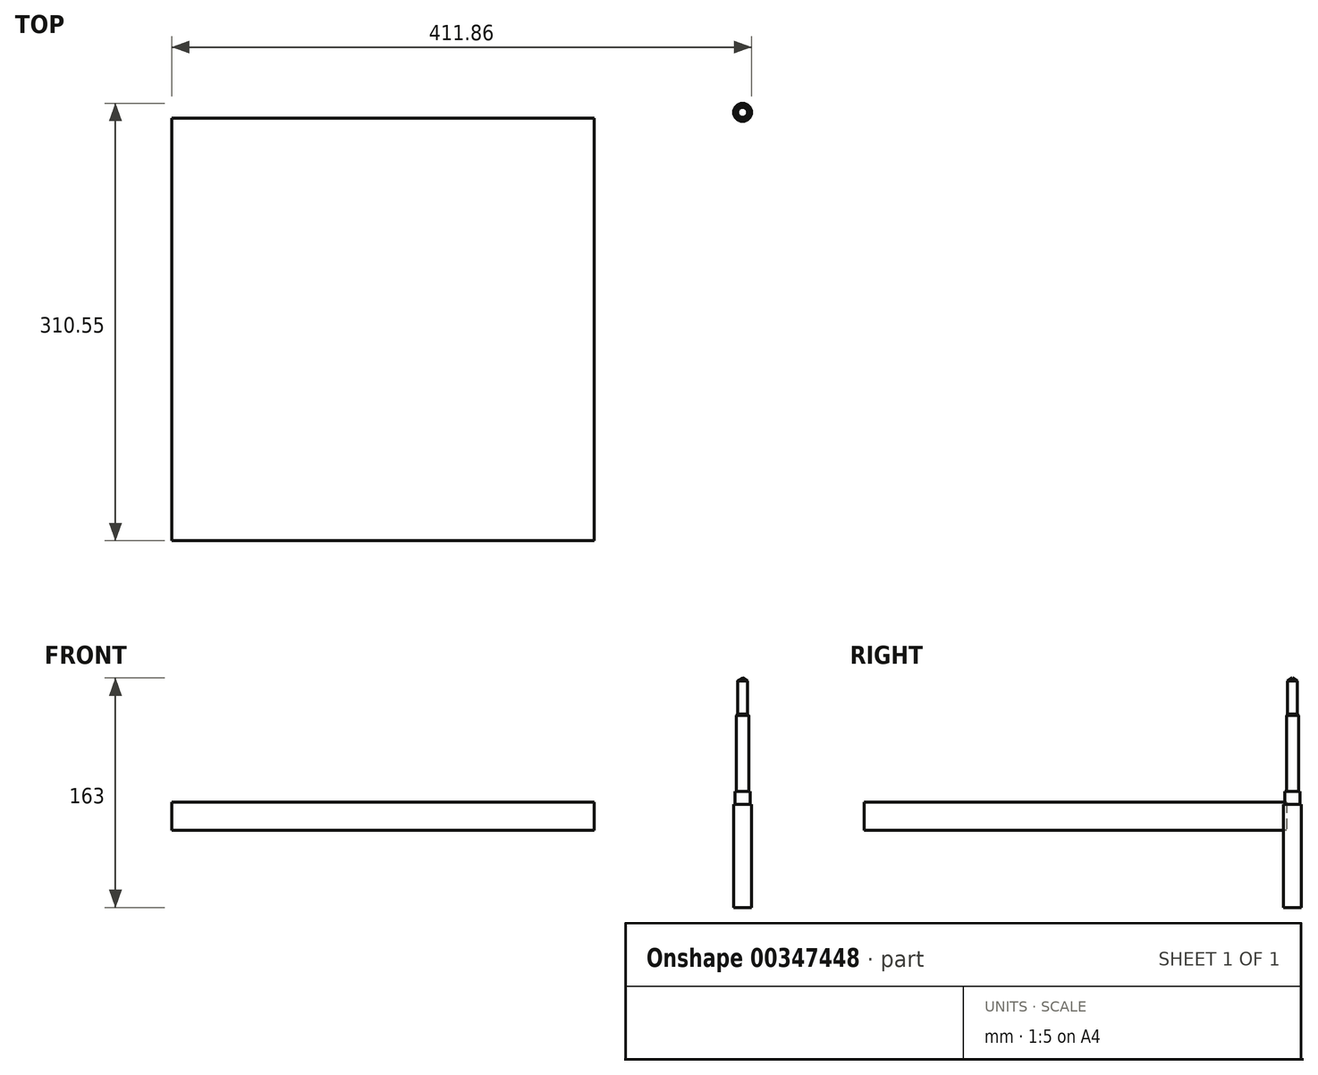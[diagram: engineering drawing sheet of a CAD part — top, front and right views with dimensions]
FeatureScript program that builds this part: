
annotation { "Feature Type Name" : "Feature", "Feature Type Description" : "" }
export const myFeature = defineFeature(function(context is Context, id is Id, definition is map)
    precondition{}
    {
        {
            var Q0;
            Q0=qCreatedBy(makeId("Front.planeOp"),FACE);
            var sketch = newSketch(context, id + "F0", { "sketchPlane" : qUnion([Q0])});
            skLineSegment(sketch, "E0", {"start": v(0, 108.35) * mm, "end": v(0, -41.65) * mm});
            skLineSegment(sketch, "E1", {"start": v(0, 108.35) * mm, "end": v(3.5, 106.35) * mm});
            skLineSegment(sketch, "E2", {"start": v(3.5, 106.35) * mm, "end": v(3.5, 82.65) * mm});
            skLineSegment(sketch, "E3", {"start": v(3.5, 82.65) * mm, "end": v(4.3, 81.65) * mm});
            skLineSegment(sketch, "E4", {"start": v(4.3, 81.65) * mm, "end": v(4.3, 27.65) * mm});
            skLineSegment(sketch, "E5", {"start": v(5.5, 27.65) * mm, "end": v(5.5, 18.65) * mm});
            skLineSegment(sketch, "E6", {"start": v(4.3, 27.65) * mm, "end": v(5.5, 27.65) * mm});
            skLineSegment(sketch, "E7", {"start": v(6.35, 18.65) * mm, "end": v(6.35, -41.65) * mm});
            skLineSegment(sketch, "E8", {"start": v(5.5, 18.65) * mm, "end": v(6.35, 18.65) * mm});
            skLineSegment(sketch, "E9", {"start": v(0, -41.65) * mm, "end": v(6.35, -41.65) * mm});
            skSolve(sketch);
        }
        {
            var Q0;
            Q0=makeQuery(id+"F0.imprint","IMPRINT",FACE,{"disambiguationData":[TD([[makeQuery(id+"F0.imprint","IMPRINT",EDGE,{"derivedFrom":sQuery(id+"F0.wireOp",EDGE,"E0")}),1.0]])]});
            var Q1;
            Q1=sQuery(id+"F0.wireOp",EDGE,"E0");
            revolve(context, id + "F1", {"entities" : qUnion([Q0]), "axis" : qUnion([Q1]), "revolveType" : RevolveType.FULL});
        }
        {
            var Q0;
            Q0=qCreatedBy(makeId("Top.planeOp"),FACE);
            var sketch = newSketch(context, id + "F2", { "sketchPlane" : qUnion([Q0])});
            skLineSegment(sketch, "E10.bottom", {"start": v(-405.51, -4.2) * mm, "end": v(-105.51, -4.2) * mm});
            skLineSegment(sketch, "E10.top", {"start": v(-405.51, -304.2) * mm, "end": v(-105.51, -304.2) * mm});
            skLineSegment(sketch, "E10.left", {"start": v(-405.51, -4.2) * mm, "end": v(-405.51, -304.2) * mm});
            skLineSegment(sketch, "E10.right", {"start": v(-105.51, -4.2) * mm, "end": v(-105.51, -304.2) * mm});
            skSolve(sketch);
        }
        {
            var Q0;
            Q0=makeQuery(id+"F2.imprint","IMPRINT",FACE,{"disambiguationData":[TD([[makeQuery(id+"F2.imprint","IMPRINT",EDGE,{"derivedFrom":sQuery(id+"F2.wireOp",EDGE,"E10.bottom")}),-1.0]])]});
            extrude(context, id + "F3", {"entities" : qUnion([Q0]), "depth" : 20 * mm});
        }
        {
            var Q0;
            Q0=makeQuery(id+"F1.opRevolve","SWEPT_FACE",FACE,{"disambiguationData":[OSD([sQuery(id+"F0.wireOp",EDGE,"E9")])]});
            extrude(context, id + "F4", {"entities" : qUnion([Q0]), "operationType" : NewBodyOperationType.ADD, "depth" : 13 * mm});
        }
    });
